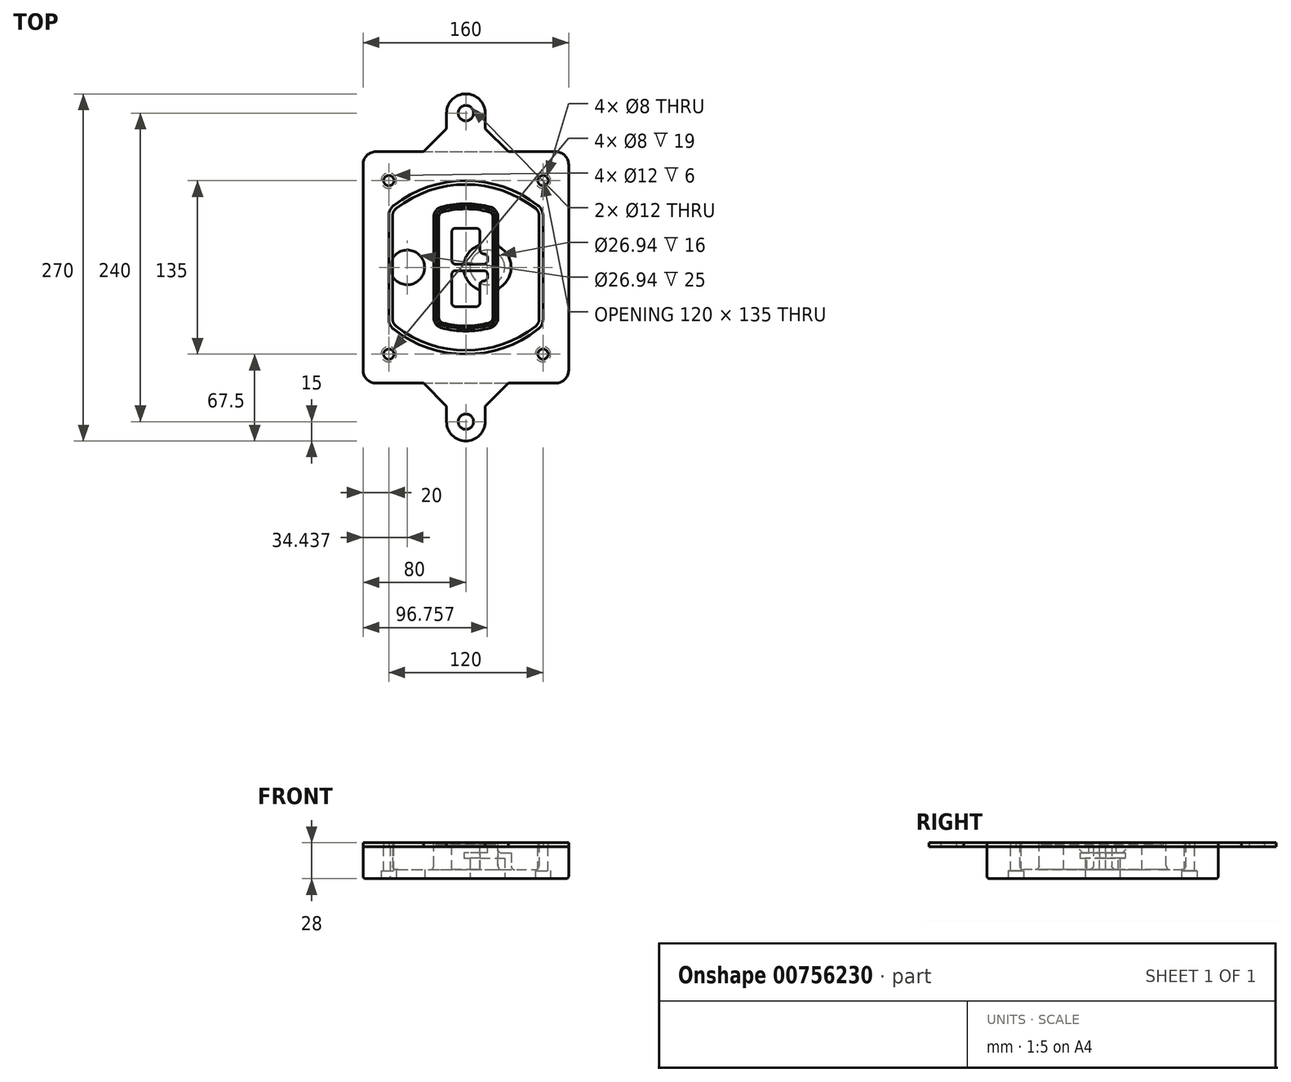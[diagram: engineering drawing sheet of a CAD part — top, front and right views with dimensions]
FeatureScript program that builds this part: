
annotation { "Feature Type Name" : "Feature", "Feature Type Description" : "" }
export const myFeature = defineFeature(function(context is Context, id is Id, definition is map)
    precondition{}
    {
        {
            var Q0;
            Q0=qCreatedBy(makeId("Top.planeOp"),FACE);
            var sketch = newSketch(context, id + "F0", { "sketchPlane" : qUnion([Q0])});
            skPoint(sketch, "E0.rect.middle", {"position": v(0, 0) * mm});
            skLineSegment(sketch, "E1.bottom", {"start": v(-70, -90) * mm, "end": v(70, -90) * mm});
            skLineSegment(sketch, "E1.top", {"start": v(-70, 90) * mm, "end": v(70, 90) * mm});
            skLineSegment(sketch, "E1.left", {"start": v(-80, -80) * mm, "end": v(-80, 80) * mm});
            skLineSegment(sketch, "E1.right", {"start": v(80, -80) * mm, "end": v(80, 80) * mm});
            skLineSegment(sketch, "E2", {"start": v(-80, 90) * mm, "end": v(80, -90) * mm, "construction": true});
            skLineSegment(sketch, "E3", {"start": v(80, 90) * mm, "end": v(-80, -90) * mm, "construction": true});
            skCircle(sketch, "E4", {"center": v(-60, 67.5) * mm, "radius": 4 * mm});
            skCircle(sketch, "E5", {"center": v(60, 67.5) * mm, "radius": 4 * mm});
            skCircle(sketch, "E6", {"center": v(60, -67.5) * mm, "radius": 4 * mm});
            skCircle(sketch, "E7", {"center": v(-60, -67.5) * mm, "radius": 4 * mm});
            skLineSegment(sketch, "E8", {"start": v(-60, 67.5) * mm, "end": v(60, 67.5) * mm, "construction": true});
            skLineSegment(sketch, "E9", {"start": v(60, 67.5) * mm, "end": v(60, -67.5) * mm, "construction": true});
            skLineSegment(sketch, "E10", {"start": v(60, -67.5) * mm, "end": v(-60, -67.5) * mm, "construction": true});
            skLineSegment(sketch, "E11", {"start": v(-60, -67.5) * mm, "end": v(-60, 67.5) * mm, "construction": true});
            skLineSegment(sketch, "E12", {"start": v(-60, 40.3) * mm, "end": v(-60, -40.3) * mm});
            skLineSegment(sketch, "E13", {"start": v(60, 40.3) * mm, "end": v(60, -40.3) * mm});
            skArc(sketch, "E14", {"start": v(56.15, 48.18) * mm, "mid": v(0, 67.5) * mm, "end": v(-56.15, 48.18) * mm});
            skArc(sketch, "E15", {"start": v(-56.15, -48.18) * mm, "mid": v(0, -67.5) * mm, "end": v(56.15, -48.18) * mm});
            skLineSegment(sketch, "E16", {"start": v(-60, 0) * mm, "end": v(60, 0) * mm, "construction": true});
            skPoint(sketch, "E17.visualSharp", {"position": v(-60, -45) * mm});
            skArc(sketch, "E17.filletArc", {"start": v(-60, -40.3) * mm, "mid": v(-58.99, -44.68) * mm, "end": v(-56.15, -48.18) * mm});
            skPoint(sketch, "E18.visualSharp", {"position": v(-60, 45) * mm});
            skArc(sketch, "E18.filletArc", {"start": v(-56.15, 48.18) * mm, "mid": v(-58.99, 44.68) * mm, "end": v(-60, 40.3) * mm});
            skPoint(sketch, "E19.visualSharp", {"position": v(60, 45) * mm});
            skArc(sketch, "E19.filletArc", {"start": v(60, 40.3) * mm, "mid": v(58.99, 44.68) * mm, "end": v(56.15, 48.18) * mm});
            skPoint(sketch, "E20.visualSharp", {"position": v(60, -45) * mm});
            skArc(sketch, "E20.filletArc", {"start": v(56.15, -48.18) * mm, "mid": v(58.99, -44.68) * mm, "end": v(60, -40.3) * mm});
            skPoint(sketch, "E21.visualSharp", {"position": v(-80, 90) * mm});
            skArc(sketch, "E21.filletArc", {"start": v(-70, 90) * mm, "mid": v(-77.07, 87.07) * mm, "end": v(-80, 80) * mm});
            skPoint(sketch, "E22.visualSharp", {"position": v(80, 90) * mm});
            skArc(sketch, "E22.filletArc", {"start": v(80, 80) * mm, "mid": v(77.07, 87.07) * mm, "end": v(70, 90) * mm});
            skPoint(sketch, "E23.visualSharp", {"position": v(80, -90) * mm});
            skArc(sketch, "E23.filletArc", {"start": v(70, -90) * mm, "mid": v(77.07, -87.07) * mm, "end": v(80, -80) * mm});
            skPoint(sketch, "E24.visualSharp", {"position": v(-80, -90) * mm});
            skArc(sketch, "E24.filletArc", {"start": v(-80, -80) * mm, "mid": v(-77.07, -87.07) * mm, "end": v(-70, -90) * mm});
            skArc(sketch, "E25.0", {"start": v(57, 40.3) * mm, "mid": v(56.3, 43.36) * mm, "end": v(54.3, 45.81) * mm});
            skLineSegment(sketch, "E25.1", {"start": v(57, 40.3) * mm, "end": v(57, -40.3) * mm});
            skArc(sketch, "E25.2", {"start": v(54.3, -45.81) * mm, "mid": v(56.3, -43.36) * mm, "end": v(57, -40.3) * mm});
            skArc(sketch, "E25.3", {"start": v(-54.3, -45.81) * mm, "mid": v(0, -64.5) * mm, "end": v(54.3, -45.81) * mm});
            skArc(sketch, "E25.4", {"start": v(-57, -40.3) * mm, "mid": v(-56.3, -43.36) * mm, "end": v(-54.3, -45.81) * mm});
            skArc(sketch, "E25.5", {"start": v(54.3, 45.81) * mm, "mid": v(0, 64.5) * mm, "end": v(-54.3, 45.81) * mm});
            skLineSegment(sketch, "E25.6", {"start": v(-57, 40.3) * mm, "end": v(-57, -40.3) * mm});
            skArc(sketch, "E25.7", {"start": v(-54.3, 45.81) * mm, "mid": v(-56.3, 43.36) * mm, "end": v(-57, 40.3) * mm});
            skArc(sketch, "E26.0", {"start": v(-58.62, 51.33) * mm, "mid": v(-62.58, 46.43) * mm, "end": v(-64, 40.3) * mm});
            skArc(sketch, "E26.1", {"start": v(58.62, 51.33) * mm, "mid": v(0, 71.5) * mm, "end": v(-58.62, 51.33) * mm});
            skArc(sketch, "E26.2", {"start": v(64, 40.3) * mm, "mid": v(62.58, 46.43) * mm, "end": v(58.62, 51.33) * mm});
            skLineSegment(sketch, "E26.3", {"start": v(64, 40.3) * mm, "end": v(64, -40.3) * mm});
            skArc(sketch, "E26.4", {"start": v(58.62, -51.33) * mm, "mid": v(62.58, -46.43) * mm, "end": v(64, -40.3) * mm});
            skLineSegment(sketch, "E26.5", {"start": v(-64, 40.3) * mm, "end": v(-64, -40.3) * mm});
            skArc(sketch, "E26.6", {"start": v(-58.62, -51.33) * mm, "mid": v(0, -71.5) * mm, "end": v(58.62, -51.33) * mm});
            skArc(sketch, "E26.7", {"start": v(-64, -40.3) * mm, "mid": v(-62.58, -46.43) * mm, "end": v(-58.62, -51.33) * mm});
            skSolve(sketch);
        }
        {
            var Q0;
            Q0=makeQuery(id+"F0.imprint","IMPRINT",FACE,{"disambiguationData":[TD([[makeQuery(id+"F0.imprint","IMPRINT",EDGE,{"derivedFrom":sQuery(id+"F0.wireOp",EDGE,"E1.bottom")}),1.0]])]});
            var Q1;
            Q1=makeQuery(id+"F0.imprint","IMPRINT",FACE,{"disambiguationData":[TD([[makeQuery(id+"F0.imprint","IMPRINT",EDGE,{"derivedFrom":sQuery(id+"F0.wireOp",EDGE,"E12")}),1.0]])]});
            var Q2;
            Q2=makeQuery(id+"F0.imprint","IMPRINT",FACE,{"disambiguationData":[TD([[makeQuery(id+"F0.imprint","IMPRINT",EDGE,{"derivedFrom":sQuery(id+"F0.wireOp",EDGE,"E25.0")}),1.0]])]});
            var Q3;
            Q3=makeQuery(id+"F0.imprint","IMPRINT",FACE,{"disambiguationData":[TD([[makeQuery(id+"F0.imprint","IMPRINT",EDGE,{"derivedFrom":sQuery(id+"F0.wireOp",EDGE,"E12")}),-1.0]])]});
            extrude(context, id + "F1", {"entities" : qUnion([Q0, Q1, Q2, Q3]), "oppositeDirection" : true, "depth" : 25 * mm});
        }
        {
            var Q0;
            Q0=makeQuery(id+"F0.imprint","IMPRINT",FACE,{"disambiguationData":[TD([[makeQuery(id+"F0.imprint","IMPRINT",EDGE,{"derivedFrom":sQuery(id+"F0.wireOp",EDGE,"E12")}),1.0]])]});
            extrude(context, id + "F2", {"entities" : qUnion([Q0]), "operationType" : NewBodyOperationType.ADD, "depth" : 3 * mm});
        }
        {
            var Q0;
            Q0=makeQuery(id+"F0.imprint","IMPRINT",FACE,{"disambiguationData":[TD([[makeQuery(id+"F0.imprint","IMPRINT",EDGE,{"derivedFrom":sQuery(id+"F0.wireOp",EDGE,"E25.0")}),1.0]])]});
            extrude(context, id + "F3", {"entities" : qUnion([Q0]), "operationType" : NewBodyOperationType.REMOVE, "oppositeDirection" : true, "depth" : 18 * mm});
        }
        {
            var Q0;
            Q0=makeQuery(id+"F2.opExtrude","CAP_FACE",FACE,{"disambiguationData":[OSD([sQuery(id+"F0.wireOp",EDGE,"E12"),sQuery(id+"F0.wireOp",EDGE,"E13"),sQuery(id+"F0.wireOp",EDGE,"E14"),sQuery(id+"F0.wireOp",EDGE,"E15"),sQuery(id+"F0.wireOp",EDGE,"E17.filletArc"),sQuery(id+"F0.wireOp",EDGE,"E18.filletArc"),sQuery(id+"F0.wireOp",EDGE,"E19.filletArc"),sQuery(id+"F0.wireOp",EDGE,"E20.filletArc"),sQuery(id+"F0.wireOp",EDGE,"E25.0"),sQuery(id+"F0.wireOp",EDGE,"E25.1"),sQuery(id+"F0.wireOp",EDGE,"E25.2"),sQuery(id+"F0.wireOp",EDGE,"E25.3"),sQuery(id+"F0.wireOp",EDGE,"E25.4"),sQuery(id+"F0.wireOp",EDGE,"E25.5"),sQuery(id+"F0.wireOp",EDGE,"E25.6"),sQuery(id+"F0.wireOp",EDGE,"E25.7")])],"isStart":false});
            var sketch = newSketch(context, id + "F4", { "sketchPlane" : qUnion([Q0])});
            skArc(sketch, "E27.0", {"start": v(-19.08, -46.97) * mm, "mid": v(0, -49.5) * mm, "end": v(19.08, -46.97) * mm});
            skArc(sketch, "E28.0", {"start": v(19.08, 46.97) * mm, "mid": v(0, 49.5) * mm, "end": v(-19.08, 46.97) * mm});
            skLineSegment(sketch, "E29", {"start": v(-25, 39.25) * mm, "end": v(-25, -39.25) * mm});
            skLineSegment(sketch, "E30", {"start": v(25, 39.25) * mm, "end": v(25, -39.25) * mm});
            skLineSegment(sketch, "E31", {"start": v(-25, 45.1) * mm, "end": v(25, 45.1) * mm, "construction": true});
            skLineSegment(sketch, "E32", {"start": v(-25, -45.1) * mm, "end": v(25, -45.1) * mm, "construction": true});
            skPoint(sketch, "E33.visualSharp", {"position": v(-25, 45.1) * mm});
            skArc(sketch, "E33.filletArc", {"start": v(-19.08, 46.97) * mm, "mid": v(-23.35, 44.11) * mm, "end": v(-25, 39.25) * mm});
            skPoint(sketch, "E34.visualSharp", {"position": v(25, 45.1) * mm});
            skArc(sketch, "E34.filletArc", {"start": v(25, 39.25) * mm, "mid": v(23.35, 44.11) * mm, "end": v(19.08, 46.97) * mm});
            skPoint(sketch, "E35.visualSharp", {"position": v(25, -45.1) * mm});
            skArc(sketch, "E35.filletArc", {"start": v(19.08, -46.97) * mm, "mid": v(23.35, -44.11) * mm, "end": v(25, -39.25) * mm});
            skPoint(sketch, "E36.visualSharp", {"position": v(-25, -45.1) * mm});
            skArc(sketch, "E36.filletArc", {"start": v(-25, -39.25) * mm, "mid": v(-23.35, -44.11) * mm, "end": v(-19.08, -46.97) * mm});
            skArc(sketch, "E37.0", {"start": v(54.3, 45.81) * mm, "mid": v(0, 64.5) * mm, "end": v(-54.3, 45.81) * mm});
            skArc(sketch, "E37.1", {"start": v(-54.3, 45.81) * mm, "mid": v(-56.3, 43.36) * mm, "end": v(-57, 40.3) * mm});
            skLineSegment(sketch, "E37.2", {"start": v(-57, 40.3) * mm, "end": v(-57, -40.3) * mm});
            skArc(sketch, "E37.3", {"start": v(-57, -40.3) * mm, "mid": v(-56.3, -43.36) * mm, "end": v(-54.3, -45.81) * mm});
            skArc(sketch, "E37.4", {"start": v(-54.3, -45.81) * mm, "mid": v(0, -64.5) * mm, "end": v(54.3, -45.81) * mm});
            skArc(sketch, "E37.5", {"start": v(54.3, -45.81) * mm, "mid": v(56.3, -43.36) * mm, "end": v(57, -40.3) * mm});
            skLineSegment(sketch, "E37.6", {"start": v(57, 40.3) * mm, "end": v(57, -40.3) * mm});
            skArc(sketch, "E37.7", {"start": v(57, 40.3) * mm, "mid": v(56.3, 43.36) * mm, "end": v(54.3, 45.81) * mm});
            skLineSegment(sketch, "E38.0", {"start": v(23, 39.25) * mm, "end": v(23, -39.25) * mm});
            skArc(sketch, "E38.1", {"start": v(18.56, -45.04) * mm, "mid": v(21.76, -42.9) * mm, "end": v(23, -39.25) * mm});
            skArc(sketch, "E38.2", {"start": v(-18.56, -45.04) * mm, "mid": v(0, -47.5) * mm, "end": v(18.56, -45.04) * mm});
            skArc(sketch, "E38.3", {"start": v(-23, -39.25) * mm, "mid": v(-21.76, -42.9) * mm, "end": v(-18.56, -45.04) * mm});
            skLineSegment(sketch, "E38.4", {"start": v(-23, 39.25) * mm, "end": v(-23, -39.25) * mm});
            skArc(sketch, "E38.5", {"start": v(23, 39.25) * mm, "mid": v(21.76, 42.9) * mm, "end": v(18.56, 45.04) * mm});
            skArc(sketch, "E38.6", {"start": v(-18.56, 45.04) * mm, "mid": v(-21.76, 42.9) * mm, "end": v(-23, 39.25) * mm});
            skArc(sketch, "E38.7", {"start": v(18.56, 45.04) * mm, "mid": v(0, 47.5) * mm, "end": v(-18.56, 45.04) * mm});
            skArc(sketch, "E39.0", {"start": v(21, 39.25) * mm, "mid": v(20.18, 41.68) * mm, "end": v(18.04, 43.1) * mm});
            skLineSegment(sketch, "E39.1", {"start": v(21, 39.25) * mm, "end": v(21, -39.25) * mm});
            skArc(sketch, "E39.2", {"start": v(18.04, -43.1) * mm, "mid": v(20.18, -41.68) * mm, "end": v(21, -39.25) * mm});
            skArc(sketch, "E39.3", {"start": v(-18.04, -43.1) * mm, "mid": v(0, -45.5) * mm, "end": v(18.04, -43.1) * mm});
            skArc(sketch, "E39.4", {"start": v(-21, -39.25) * mm, "mid": v(-20.18, -41.68) * mm, "end": v(-18.04, -43.1) * mm});
            skArc(sketch, "E39.5", {"start": v(18.04, 43.1) * mm, "mid": v(0, 45.5) * mm, "end": v(-18.04, 43.1) * mm});
            skLineSegment(sketch, "E39.6", {"start": v(-21, 39.25) * mm, "end": v(-21, -39.25) * mm});
            skArc(sketch, "E39.7", {"start": v(-18.04, 43.1) * mm, "mid": v(-20.18, 41.68) * mm, "end": v(-21, 39.25) * mm});
            skLineSegment(sketch, "E40", {"start": v(-25, 0) * mm, "end": v(25, 0) * mm, "construction": true});
            skLineSegment(sketch, "E41", {"start": v(-11, 5.5) * mm, "end": v(-11, 27.5) * mm});
            skLineSegment(sketch, "E42", {"start": v(-8, 30.5) * mm, "end": v(8, 30.5) * mm});
            skLineSegment(sketch, "E43", {"start": v(11, 27.5) * mm, "end": v(11, 13.5) * mm});
            skLineSegment(sketch, "E44", {"start": v(14, 10.5) * mm, "end": v(14, 10.5) * mm});
            skLineSegment(sketch, "E45", {"start": v(17, 7.5) * mm, "end": v(17, 5.5) * mm});
            skLineSegment(sketch, "E46", {"start": v(14, 2.5) * mm, "end": v(-8, 2.5) * mm});
            skPoint(sketch, "E47.visualSharp", {"position": v(-11, 30.5) * mm});
            skArc(sketch, "E47.filletArc", {"start": v(-8, 30.5) * mm, "mid": v(-10.12, 29.62) * mm, "end": v(-11, 27.5) * mm});
            skPoint(sketch, "E48.visualSharp", {"position": v(11, 30.5) * mm});
            skArc(sketch, "E48.filletArc", {"start": v(11, 27.5) * mm, "mid": v(10.12, 29.62) * mm, "end": v(8, 30.5) * mm});
            skPoint(sketch, "E49.visualSharp", {"position": v(11, 10.5) * mm});
            skArc(sketch, "E49.filletArc", {"start": v(11, 13.5) * mm, "mid": v(11.88, 11.38) * mm, "end": v(14, 10.5) * mm});
            skPoint(sketch, "E50.visualSharp", {"position": v(17, 10.5) * mm});
            skArc(sketch, "E50.filletArc", {"start": v(17, 7.5) * mm, "mid": v(16.12, 9.62) * mm, "end": v(14, 10.5) * mm});
            skPoint(sketch, "E51.visualSharp", {"position": v(17, 2.5) * mm});
            skArc(sketch, "E51.filletArc", {"start": v(14, 2.5) * mm, "mid": v(16.12, 3.38) * mm, "end": v(17, 5.5) * mm});
            skPoint(sketch, "E52.visualSharp", {"position": v(-11, 2.5) * mm});
            skArc(sketch, "E52.filletArc", {"start": v(-11, 5.5) * mm, "mid": v(-10.12, 3.38) * mm, "end": v(-8, 2.5) * mm});
            skLineSegment(sketch, "E53.0.MirrorCS", {"start": v(14, -2.5) * mm, "end": v(-8, -2.5) * mm});
            skArc(sketch, "E54.0.MirrorCS", {"start": v(-11, -5.5) * mm, "mid": v(-10.12, -3.38) * mm, "end": v(-8, -2.5) * mm});
            skLineSegment(sketch, "E55.0.MirrorCS", {"start": v(-11, -5.5) * mm, "end": v(-11, -27.5) * mm});
            skArc(sketch, "E56.0.MirrorCS", {"start": v(-8, -30.5) * mm, "mid": v(-10.12, -29.62) * mm, "end": v(-11, -27.5) * mm});
            skLineSegment(sketch, "E57.0.MirrorCS", {"start": v(-8, -30.5) * mm, "end": v(8, -30.5) * mm});
            skArc(sketch, "E58.0.MirrorCS", {"start": v(11, -27.5) * mm, "mid": v(10.12, -29.62) * mm, "end": v(8, -30.5) * mm});
            skLineSegment(sketch, "E59.0.MirrorCS", {"start": v(11, -27.5) * mm, "end": v(11, -13.5) * mm});
            skArc(sketch, "E60.0.MirrorCS", {"start": v(11, -13.5) * mm, "mid": v(11.88, -11.38) * mm, "end": v(14, -10.5) * mm});
            skArc(sketch, "E61.0.MirrorCS", {"start": v(17, -7.5) * mm, "mid": v(16.12, -9.62) * mm, "end": v(14, -10.5) * mm});
            skLineSegment(sketch, "E62.0.MirrorCS", {"start": v(17, -7.5) * mm, "end": v(17, -5.5) * mm});
            skArc(sketch, "E63.0.MirrorCS", {"start": v(14, -2.5) * mm, "mid": v(16.12, -3.38) * mm, "end": v(17, -5.5) * mm});
            skSolve(sketch);
        }
        {
            var Q0;
            Q0=makeQuery(id+"F4.imprint","IMPRINT",FACE,{"disambiguationData":[TD([[makeQuery(id+"F4.imprint","IMPRINT",EDGE,{"derivedFrom":sQuery(id+"F4.wireOp",EDGE,"E27.0")}),1.0]])]});
            var Q1;
            Q1=makeQuery(id+"F4.imprint","IMPRINT",FACE,{"disambiguationData":[TD([[makeQuery(id+"F4.imprint","IMPRINT",EDGE,{"derivedFrom":sQuery(id+"F4.wireOp",EDGE,"E38.0")}),-1.0]])]});
            var Q2;
            Q2=makeQuery(id+"F4.imprint","IMPRINT",FACE,{"disambiguationData":[TD([[makeQuery(id+"F4.imprint","IMPRINT",EDGE,{"derivedFrom":sQuery(id+"F4.wireOp",EDGE,"E39.0")}),1.0]])]});
            extrude(context, id + "F5", {"entities" : qUnion([Q0, Q1, Q2]), "operationType" : NewBodyOperationType.ADD, "endBound" : BoundingType.UP_TO_NEXT, "oppositeDirection" : true, "depth" : 25 * mm});
        }
        {
            var Q0;
            Q0=makeQuery(id+"F4.imprint","IMPRINT",FACE,{"disambiguationData":[TD([[makeQuery(id+"F4.imprint","IMPRINT",EDGE,{"derivedFrom":sQuery(id+"F4.wireOp",EDGE,"E38.0")}),-1.0]])]});
            extrude(context, id + "F6", {"entities" : qUnion([Q0]), "operationType" : NewBodyOperationType.REMOVE, "oppositeDirection" : true, "depth" : 2 * mm});
        }
        {
            var Q0;
            Q0=makeQuery(id+"F1.opExtrude","CAP_FACE",FACE,{"disambiguationData":[OSD([sQuery(id+"F0.wireOp",EDGE,"E1.bottom"),sQuery(id+"F0.wireOp",EDGE,"E1.top"),sQuery(id+"F0.wireOp",EDGE,"E1.left"),sQuery(id+"F0.wireOp",EDGE,"E1.right"),sQuery(id+"F0.wireOp",EDGE,"E4"),sQuery(id+"F0.wireOp",EDGE,"E5"),sQuery(id+"F0.wireOp",EDGE,"E6"),sQuery(id+"F0.wireOp",EDGE,"E7"),sQuery(id+"F0.wireOp",EDGE,"E21.filletArc"),sQuery(id+"F0.wireOp",EDGE,"E22.filletArc"),sQuery(id+"F0.wireOp",EDGE,"E23.filletArc"),sQuery(id+"F0.wireOp",EDGE,"E24.filletArc")])],"isStart":false});
            var sketch = newSketch(context, id + "F7", { "sketchPlane" : qUnion([Q0])});
            skCircle(sketch, "E64", {"center": v(16.76, 0) * mm, "radius": 13.47 * mm});
            skCircle(sketch, "E65", {"center": v(-45.56, 0) * mm, "radius": 13.47 * mm});
            skLineSegment(sketch, "E66", {"start": v(80, 0) * mm, "end": v(-80, 0) * mm});
            skCircle(sketch, "E67", {"center": v(16.76, 0) * mm, "radius": 18.47 * mm});
            skCircle(sketch, "E68", {"center": v(60, -67.5) * mm, "radius": 6 * mm});
            skCircle(sketch, "E69", {"center": v(-60, -67.5) * mm, "radius": 6 * mm});
            skCircle(sketch, "E70", {"center": v(-60, 67.5) * mm, "radius": 6 * mm});
            skCircle(sketch, "E71", {"center": v(60, 67.5) * mm, "radius": 6 * mm});
            skSolve(sketch);
        }
        {
            var Q0;
            {var subQ1=sQuery(id+"F7.wireOp",EDGE,"E66");var subQ4=sQuery(id+"F7.wireOp",EDGE,"E64");var subQ6=makeQuery(id+"F7.imprint","INTERSECT",VERTEX,{"disambiguationData":[OD(0.0)],"derivedFrom":[subQ4,subQ1]});Q0=makeQuery(id+"F7.imprint","IMPRINT",FACE,{"disambiguationData":[TD([[makeQuery(id+"F7.imprint","IMPRINT",EDGE,{"disambiguationData":[TD([[subQ6,-1.0]])],"derivedFrom":subQ4}),-1.0]])]});}
            var Q1;
            {var subQ0=sQuery(id+"F7.wireOp",EDGE,"E66");var subQ1=sQuery(id+"F7.wireOp",EDGE,"E64");var subQ3=makeQuery(id+"F7.imprint","INTERSECT",VERTEX,{"disambiguationData":[OD(0.0)],"derivedFrom":[subQ1,subQ0]});Q1=makeQuery(id+"F7.imprint","IMPRINT",FACE,{"disambiguationData":[TD([[makeQuery(id+"F7.imprint","IMPRINT",EDGE,{"disambiguationData":[TD([[subQ3,-1.0]])],"derivedFrom":subQ1}),1.0]])]});}
            var Q2;
            {var subQ0=sQuery(id+"F7.wireOp",EDGE,"E66");var subQ1=sQuery(id+"F7.wireOp",EDGE,"E64");var subQ3=makeQuery(id+"F7.imprint","INTERSECT",VERTEX,{"disambiguationData":[OD(0.0)],"derivedFrom":[subQ1,subQ0]});Q2=makeQuery(id+"F7.imprint","IMPRINT",FACE,{"disambiguationData":[TD([[makeQuery(id+"F7.imprint","IMPRINT",EDGE,{"disambiguationData":[TD([[subQ3,1.0]])],"derivedFrom":subQ1}),1.0]])]});}
            var Q3;
            {var subQ1=sQuery(id+"F7.wireOp",EDGE,"E66");var subQ4=sQuery(id+"F7.wireOp",EDGE,"E64");var subQ6=makeQuery(id+"F7.imprint","INTERSECT",VERTEX,{"disambiguationData":[OD(0.0)],"derivedFrom":[subQ4,subQ1]});Q3=makeQuery(id+"F7.imprint","IMPRINT",FACE,{"disambiguationData":[TD([[makeQuery(id+"F7.imprint","IMPRINT",EDGE,{"disambiguationData":[TD([[subQ6,1.0]])],"derivedFrom":subQ4}),-1.0]])]});}
            extrude(context, id + "F8", {"entities" : qUnion([Q0, Q1, Q2, Q3]), "operationType" : NewBodyOperationType.ADD, "oppositeDirection" : true, "depth" : 20 * mm});
        }
        {
            var Q0;
            {var subQ0=sQuery(id+"F7.wireOp",EDGE,"E66");var subQ1=sQuery(id+"F7.wireOp",EDGE,"E64");var subQ3=makeQuery(id+"F7.imprint","INTERSECT",VERTEX,{"disambiguationData":[OD(0.0)],"derivedFrom":[subQ1,subQ0]});Q0=makeQuery(id+"F7.imprint","IMPRINT",FACE,{"disambiguationData":[TD([[makeQuery(id+"F7.imprint","IMPRINT",EDGE,{"disambiguationData":[TD([[subQ3,-1.0]])],"derivedFrom":subQ1}),1.0]])]});}
            var Q1;
            {var subQ0=sQuery(id+"F7.wireOp",EDGE,"E66");var subQ1=sQuery(id+"F7.wireOp",EDGE,"E64");var subQ3=makeQuery(id+"F7.imprint","INTERSECT",VERTEX,{"disambiguationData":[OD(0.0)],"derivedFrom":[subQ1,subQ0]});Q1=makeQuery(id+"F7.imprint","IMPRINT",FACE,{"disambiguationData":[TD([[makeQuery(id+"F7.imprint","IMPRINT",EDGE,{"disambiguationData":[TD([[subQ3,1.0]])],"derivedFrom":subQ1}),1.0]])]});}
            extrude(context, id + "F9", {"entities" : qUnion([Q0, Q1]), "operationType" : NewBodyOperationType.REMOVE, "oppositeDirection" : true, "depth" : 16 * mm});
        }
        {
            var Q0;
            {var subQ0=sQuery(id+"F7.wireOp",EDGE,"E66");var subQ1=sQuery(id+"F7.wireOp",EDGE,"E65");var subQ3=makeQuery(id+"F7.imprint","INTERSECT",VERTEX,{"disambiguationData":[OD(0.0)],"derivedFrom":[subQ1,subQ0]});Q0=makeQuery(id+"F7.imprint","IMPRINT",FACE,{"disambiguationData":[TD([[makeQuery(id+"F7.imprint","IMPRINT",EDGE,{"disambiguationData":[TD([[subQ3,-1.0]])],"derivedFrom":subQ1}),1.0]])]});}
            var Q1;
            {var subQ0=sQuery(id+"F7.wireOp",EDGE,"E66");var subQ1=sQuery(id+"F7.wireOp",EDGE,"E65");var subQ3=makeQuery(id+"F7.imprint","INTERSECT",VERTEX,{"disambiguationData":[OD(0.0)],"derivedFrom":[subQ1,subQ0]});Q1=makeQuery(id+"F7.imprint","IMPRINT",FACE,{"disambiguationData":[TD([[makeQuery(id+"F7.imprint","IMPRINT",EDGE,{"disambiguationData":[TD([[subQ3,1.0]])],"derivedFrom":subQ1}),1.0]])]});}
            extrude(context, id + "F10", {"entities" : qUnion([Q0, Q1]), "operationType" : NewBodyOperationType.REMOVE, "oppositeDirection" : true, "depth" : 25 * mm});
        }
        {
            var Q0;
            Q0=makeQuery(id+"F7.imprint","IMPRINT",FACE,{"disambiguationData":[TD([[makeQuery(id+"F7.imprint","IMPRINT",EDGE,{"derivedFrom":sQuery(id+"F7.wireOp",EDGE,"E68")}),1.0]])]});
            var Q1;
            Q1=makeQuery(id+"F7.imprint","IMPRINT",FACE,{"disambiguationData":[TD([[makeQuery(id+"F7.imprint","IMPRINT",EDGE,{"derivedFrom":makeQuery(id+"F1.opExtrude","CAP_EDGE",EDGE,{"disambiguationData":[OSD([sQuery(id+"F0.wireOp",EDGE,"E5")])],"isStart":false})}),-1.0]])]});
            var Q2;
            Q2=makeQuery(id+"F7.imprint","IMPRINT",FACE,{"disambiguationData":[TD([[makeQuery(id+"F7.imprint","IMPRINT",EDGE,{"derivedFrom":sQuery(id+"F7.wireOp",EDGE,"E69")}),1.0]])]});
            var Q3;
            Q3=makeQuery(id+"F7.imprint","IMPRINT",FACE,{"disambiguationData":[TD([[makeQuery(id+"F7.imprint","IMPRINT",EDGE,{"derivedFrom":makeQuery(id+"F1.opExtrude","CAP_EDGE",EDGE,{"disambiguationData":[OSD([sQuery(id+"F0.wireOp",EDGE,"E4")])],"isStart":false})}),-1.0]])]});
            var Q4;
            Q4=makeQuery(id+"F7.imprint","IMPRINT",FACE,{"disambiguationData":[TD([[makeQuery(id+"F7.imprint","IMPRINT",EDGE,{"derivedFrom":sQuery(id+"F7.wireOp",EDGE,"E70")}),1.0]])]});
            var Q5;
            Q5=makeQuery(id+"F7.imprint","IMPRINT",FACE,{"disambiguationData":[TD([[makeQuery(id+"F7.imprint","IMPRINT",EDGE,{"derivedFrom":makeQuery(id+"F1.opExtrude","CAP_EDGE",EDGE,{"disambiguationData":[OSD([sQuery(id+"F0.wireOp",EDGE,"E7")])],"isStart":false})}),-1.0]])]});
            var Q6;
            Q6=makeQuery(id+"F7.imprint","IMPRINT",FACE,{"disambiguationData":[TD([[makeQuery(id+"F7.imprint","IMPRINT",EDGE,{"derivedFrom":sQuery(id+"F7.wireOp",EDGE,"E71")}),1.0]])]});
            var Q7;
            Q7=makeQuery(id+"F7.imprint","IMPRINT",FACE,{"disambiguationData":[TD([[makeQuery(id+"F7.imprint","IMPRINT",EDGE,{"derivedFrom":makeQuery(id+"F1.opExtrude","CAP_EDGE",EDGE,{"disambiguationData":[OSD([sQuery(id+"F0.wireOp",EDGE,"E6")])],"isStart":false})}),-1.0]])]});
            extrude(context, id + "F11", {"entities" : qUnion([Q0, Q1, Q2, Q3, Q4, Q5, Q6, Q7]), "operationType" : NewBodyOperationType.REMOVE, "oppositeDirection" : true, "depth" : 6 * mm});
        }
        {
            var Q0;
            Q0=makeQuery(id+"F9.boolean.opBoolean","COPY",FACE,{"derivedFrom":makeQuery(id+"F9.opExtrude","CAP_FACE",FACE,{"disambiguationData":[OSD([sQuery(id+"F7.wireOp",EDGE,"E64")])],"isStart":false})});
            var sketch = newSketch(context, id + "F12", { "sketchPlane" : qUnion([Q0])});
            skArc(sketch, "E72.0", {"start": v(11, 17.55) * mm, "mid": v(2.57, 11.82) * mm, "end": v(-1.54, 2.5) * mm});
            skArc(sketch, "E72.1", {"start": v(-1.54, -2.5) * mm, "mid": v(2.57, -11.82) * mm, "end": v(11, -17.55) * mm});
            skLineSegment(sketch, "E73", {"start": v(-1.54, -2.5) * mm, "end": v(14, -2.5) * mm});
            skLineSegment(sketch, "E74.0", {"start": v(14, 2.5) * mm, "end": v(-1.54, 2.5) * mm});
            skArc(sketch, "E74.1", {"start": v(14, 2.5) * mm, "mid": v(16.12, 3.38) * mm, "end": v(17, 5.5) * mm});
            skLineSegment(sketch, "E74.2", {"start": v(17, 7.5) * mm, "end": v(17, 5.5) * mm});
            skArc(sketch, "E74.3", {"start": v(17, 7.5) * mm, "mid": v(16.12, 9.62) * mm, "end": v(14, 10.5) * mm});
            skArc(sketch, "E74.4", {"start": v(11, 13.5) * mm, "mid": v(11.88, 11.38) * mm, "end": v(14, 10.5) * mm});
            skLineSegment(sketch, "E74.5", {"start": v(11, 17.55) * mm, "end": v(11, 13.5) * mm});
            skLineSegment(sketch, "E74.7", {"start": v(14, -2.5) * mm, "end": v(-1.54, -2.5) * mm});
            skArc(sketch, "E74.8", {"start": v(14, -2.5) * mm, "mid": v(16.12, -3.38) * mm, "end": v(17, -5.5) * mm});
            skLineSegment(sketch, "E74.9", {"start": v(17, -7.5) * mm, "end": v(17, -5.5) * mm});
            skArc(sketch, "E74.10", {"start": v(17, -7.5) * mm, "mid": v(16.12, -9.62) * mm, "end": v(14, -10.5) * mm});
            skArc(sketch, "E74.11", {"start": v(11, -13.5) * mm, "mid": v(11.88, -11.38) * mm, "end": v(14, -10.5) * mm});
            skLineSegment(sketch, "E74.12", {"start": v(11, -17.55) * mm, "end": v(11, -13.5) * mm});
            skPoint(sketch, "E75.orphan", {"position": v(11, -27.5) * mm});
            skPoint(sketch, "E76.orphan", {"position": v(-8, -2.5) * mm});
            skPoint(sketch, "E77.orphan", {"position": v(-8, 2.5) * mm});
            skPoint(sketch, "E78.orphan", {"position": v(11, 27.5) * mm});
            skSolve(sketch);
        }
        {
            var Q0;
            {var subQ7=sQuery(id+"F12.wireOp",EDGE,"E72.0");var subQ14=sQuery(id+"F12.wireOp",EDGE,"E72.1");var subQ16=sQuery(id+"F12.wireOp",EDGE,"E74.1");var subQ18=sQuery(id+"F12.wireOp",EDGE,"E74.8");Q0=qUnion([makeQuery(id+"F12.imprint","IMPRINT",FACE,{"disambiguationData":[TD([[makeQuery(id+"F12.imprint","IMPRINT",EDGE,{"derivedFrom":subQ7}),1.0]])]}),makeQuery(id+"F12.imprint","IMPRINT",FACE,{"disambiguationData":[TD([[makeQuery(id+"F12.imprint","IMPRINT",EDGE,{"derivedFrom":subQ14}),1.0]])]}),makeQuery(id+"F12.imprint","IMPRINT",FACE,{"disambiguationData":[TD([[makeQuery(id+"F12.imprint","IMPRINT",EDGE,{"derivedFrom":subQ16}),1.0]])]}),makeQuery(id+"F12.imprint","IMPRINT",FACE,{"disambiguationData":[TD([[makeQuery(id+"F12.imprint","IMPRINT",EDGE,{"derivedFrom":subQ18}),-1.0]])]})]);}
            var Q1;
            Q1=makeQuery(id+"F5.boolean.opBoolean","SPLIT",FACE,{"disambiguationData":[TD([makeQuery(id+"F5.opExtrude","SWEPT_FACE",FACE,{"disambiguationData":[OSD([sQuery(id+"F4.wireOp",EDGE,"E41")])]})])],"derivedFrom":makeQuery(id+"F3.boolean.opBoolean","COPY",FACE,{"derivedFrom":makeQuery(id+"F3.opExtrude","CAP_FACE",FACE,{"disambiguationData":[OSD([sQuery(id+"F0.wireOp",EDGE,"E25.0"),sQuery(id+"F0.wireOp",EDGE,"E25.1"),sQuery(id+"F0.wireOp",EDGE,"E25.2"),sQuery(id+"F0.wireOp",EDGE,"E25.3"),sQuery(id+"F0.wireOp",EDGE,"E25.4"),sQuery(id+"F0.wireOp",EDGE,"E25.5"),sQuery(id+"F0.wireOp",EDGE,"E25.6"),sQuery(id+"F0.wireOp",EDGE,"E25.7")])],"isStart":false})})});
            extrude(context, id + "F13", {"entities" : qUnion([Q0]), "operationType" : NewBodyOperationType.REMOVE, "endBound" : BoundingType.UP_TO_SURFACE, "endBoundEntityFace" : qUnion([Q1]), "depth" : 25 * mm});
        }
        {
            var Q0;
            Q0=makeQuery(id+"F3.boolean.opBoolean","COPY",EDGE,{"derivedFrom":makeQuery(id+"F3.opExtrude","CAP_EDGE",EDGE,{"disambiguationData":[OSD([sQuery(id+"F0.wireOp",EDGE,"E25.6")])],"isStart":false})});
            var Q1;
            Q1=makeQuery(id+"F8.boolean.opBoolean","INTERSECT",EDGE,{"derivedFrom":[makeQuery(id+"F5.opExtrude","SWEPT_FACE",FACE,{"disambiguationData":[OSD([sQuery(id+"F4.wireOp",EDGE,"E30")])]}),makeQuery(id+"F8.opExtrude","CAP_FACE",FACE,{"disambiguationData":[OSD([sQuery(id+"F7.wireOp",EDGE,"E67")])],"isStart":false})]});
            var Q2;
            Q2=makeQuery(id+"F8.boolean.opBoolean","INTERSECT",EDGE,{"disambiguationData":[OD(1.0)],"derivedFrom":[makeQuery(id+"F5.opExtrude","SWEPT_FACE",FACE,{"disambiguationData":[OSD([sQuery(id+"F4.wireOp",EDGE,"E30")])]}),makeQuery(id+"F8.opExtrude","SWEPT_FACE",FACE,{"disambiguationData":[OSD([sQuery(id+"F7.wireOp",EDGE,"E67")])]})]});
            var Q3;
            {var subQ0=sQuery(id+"F4.wireOp",EDGE,"E30");Q3=makeQuery(id+"F8.boolean.opBoolean","SPLIT",EDGE,{"disambiguationData":[TD([makeQuery(id+"F5.opExtrude","SWEPT_FACE",FACE,{"disambiguationData":[OSD([sQuery(id+"F4.wireOp",EDGE,"E35.filletArc")])]})])],"derivedFrom":makeQuery(id+"F5.opExtrude","CAP_EDGE",EDGE,{"disambiguationData":[OSD([subQ0])],"isStart":false})});}
            var Q4;
            {var subQ0=sQuery(id+"F0.wireOp",EDGE,"E25.7");var subQ1=sQuery(id+"F0.wireOp",EDGE,"E25.1");var subQ2=sQuery(id+"F0.wireOp",EDGE,"E25.6");var subQ3=sQuery(id+"F0.wireOp",EDGE,"E25.5");var subQ4=sQuery(id+"F0.wireOp",EDGE,"E25.4");var subQ5=sQuery(id+"F0.wireOp",EDGE,"E25.0");var subQ6=sQuery(id+"F0.wireOp",EDGE,"E25.2");var subQ7=sQuery(id+"F0.wireOp",EDGE,"E25.3");Q4=makeQuery(id+"F8.boolean.opBoolean","INTERSECT",EDGE,{"derivedFrom":[makeQuery(id+"F5.boolean.opBoolean","SPLIT",FACE,{"disambiguationData":[TD([makeQuery(id+"F2.opExtrude","SWEPT_FACE",FACE,{"disambiguationData":[OSD([subQ5])]})])],"derivedFrom":makeQuery(id+"F3.boolean.opBoolean","COPY",FACE,{"derivedFrom":makeQuery(id+"F3.opExtrude","CAP_FACE",FACE,{"disambiguationData":[OSD([subQ5,subQ1,subQ6,subQ7,subQ4,subQ3,subQ2,subQ0])],"isStart":false})})}),makeQuery(id+"F8.opExtrude","SWEPT_FACE",FACE,{"disambiguationData":[OSD([sQuery(id+"F7.wireOp",EDGE,"E67")])]})]});}
            var Q5;
            Q5=makeQuery(id+"F8.boolean.opBoolean","INTERSECT",EDGE,{"disambiguationData":[OD(0.0)],"derivedFrom":[makeQuery(id+"F5.opExtrude","SWEPT_FACE",FACE,{"disambiguationData":[OSD([sQuery(id+"F4.wireOp",EDGE,"E30")])]}),makeQuery(id+"F8.opExtrude","SWEPT_FACE",FACE,{"disambiguationData":[OSD([sQuery(id+"F7.wireOp",EDGE,"E67")])]})]});
            fillet(context, id + "F14", {"entities" : qUnion([Q0, Q1, Q2, Q3, Q4, Q5]), "radius" : 3 * mm, "tangentPropagation" : true, "allowEdgeOverflow" : false});
        }
        {
            var Q0;
            Q0=makeQuery(id+"F1.opExtrude","CAP_EDGE",EDGE,{"disambiguationData":[OSD([sQuery(id+"F0.wireOp",EDGE,"E1.bottom")])],"isStart":false});
            fillet(context, id + "F15", {"entities" : qUnion([Q0]), "radius" : 2 * mm, "tangentPropagation" : true, "allowEdgeOverflow" : false});
        }
        {
            var Q0;
            {var subQ0=sQuery(id+"F0.wireOp",EDGE,"E21.filletArc");var subQ1=sQuery(id+"F0.wireOp",EDGE,"E7");var subQ2=sQuery(id+"F0.wireOp",EDGE,"E6");var subQ3=sQuery(id+"F0.wireOp",EDGE,"E5");var subQ4=sQuery(id+"F0.wireOp",EDGE,"E4");var subQ5=sQuery(id+"F0.wireOp",EDGE,"E22.filletArc");var subQ6=sQuery(id+"F0.wireOp",EDGE,"E1.bottom");var subQ7=sQuery(id+"F0.wireOp",EDGE,"E1.right");var subQ8=sQuery(id+"F0.wireOp",EDGE,"E1.top");var subQ9=sQuery(id+"F0.wireOp",EDGE,"E1.left");var subQ10=sQuery(id+"F0.wireOp",EDGE,"E23.filletArc");var subQ11=sQuery(id+"F0.wireOp",EDGE,"E24.filletArc");Q0=makeQuery(id+"F2.boolean.opBoolean","SPLIT",FACE,{"disambiguationData":[TD([makeQuery(id+"F1.opExtrude","SWEPT_FACE",FACE,{"disambiguationData":[OSD([subQ6])]})])],"derivedFrom":makeQuery(id+"F1.opExtrude","CAP_FACE",FACE,{"disambiguationData":[OSD([subQ6,subQ8,subQ9,subQ7,subQ4,subQ3,subQ2,subQ1,subQ0,subQ5,subQ10,subQ11])],"isStart":true})});}
            var sketch = newSketch(context, id + "F16", { "sketchPlane" : qUnion([Q0])});
            skPoint(sketch, "E79.startSnap0", {"position": v(0, 90) * mm});
            skLineSegment(sketch, "E80", {"start": v(0, 90) * mm, "end": v(0, 120) * mm, "construction": true});
            skCircle(sketch, "E81", {"center": v(0, 120) * mm, "radius": 6 * mm});
            skLineSegment(sketch, "E82", {"start": v(15, 120) * mm, "end": v(15, 108) * mm});
            skLineSegment(sketch, "E83", {"start": v(15, 108) * mm, "end": v(33, 90) * mm});
            skLineSegment(sketch, "E84", {"start": v(33, 90) * mm, "end": v(-33, 90) * mm});
            skLineSegment(sketch, "E85", {"start": v(-33, 90) * mm, "end": v(-15, 108) * mm});
            skLineSegment(sketch, "E86", {"start": v(-15, 108) * mm, "end": v(-15, 120) * mm});
            skArc(sketch, "E87", {"start": v(15, 120) * mm, "mid": v(0, 135) * mm, "end": v(-15, 120) * mm});
            skLineSegment(sketch, "E88", {"start": v(80, 0) * mm, "end": v(-80, 0) * mm, "construction": true});
            skLineSegment(sketch, "E89.MirrorCS", {"start": v(15, -108) * mm, "end": v(33, -90) * mm});
            skLineSegment(sketch, "E90.MirrorCS", {"start": v(15, -120) * mm, "end": v(15, -108) * mm});
            skArc(sketch, "E91.MirrorCS", {"start": v(15, -120) * mm, "mid": v(0, -135) * mm, "end": v(-15, -120) * mm});
            skCircle(sketch, "E92.MirrorC", {"center": v(0, -120) * mm, "radius": 6 * mm});
            skLineSegment(sketch, "E93.MirrorCS", {"start": v(-33, -90) * mm, "end": v(-15, -108) * mm});
            skLineSegment(sketch, "E94.MirrorCS", {"start": v(-15, -108) * mm, "end": v(-15, -120) * mm});
            skLineSegment(sketch, "E95.MirrorCS", {"start": v(33, -90) * mm, "end": v(-33, -90) * mm});
            skLineSegment(sketch, "E96.MirrorCS", {"start": v(0, -90) * mm, "end": v(0, -120) * mm, "construction": true});
            skSolve(sketch);
        }
        {
            var Q0;
            Q0=makeQuery(id+"F16.imprint","IMPRINT",FACE,{"disambiguationData":[TD([[makeQuery(id+"F16.imprint","IMPRINT",EDGE,{"derivedFrom":sQuery(id+"F16.wireOp",EDGE,"E81")}),-1.0]])]});
            var Q1;
            {var subQ4=sQuery(id+"F16.wireOp",EDGE,"E84");Q1=makeQuery(id+"F16.imprint","IMPRINT",FACE,{"disambiguationData":[TD([[makeQuery(id+"F16.imprint","IMPRINT",EDGE,{"derivedFrom":subQ4}),-1.0]])]});}
            var Q2;
            Q2=makeQuery(id+"F16.imprint","IMPRINT",FACE,{"disambiguationData":[TD([[makeQuery(id+"F16.imprint","IMPRINT",EDGE,{"derivedFrom":sQuery(id+"F16.wireOp",EDGE,"E89.MirrorCS")}),1.0]])]});
            var Q3;
            Q3=makeQuery(id+"F2.opExtrude","CAP_FACE",FACE,{"disambiguationData":[OSD([sQuery(id+"F0.wireOp",EDGE,"E12"),sQuery(id+"F0.wireOp",EDGE,"E13"),sQuery(id+"F0.wireOp",EDGE,"E14"),sQuery(id+"F0.wireOp",EDGE,"E15"),sQuery(id+"F0.wireOp",EDGE,"E17.filletArc"),sQuery(id+"F0.wireOp",EDGE,"E18.filletArc"),sQuery(id+"F0.wireOp",EDGE,"E19.filletArc"),sQuery(id+"F0.wireOp",EDGE,"E20.filletArc"),sQuery(id+"F0.wireOp",EDGE,"E25.0"),sQuery(id+"F0.wireOp",EDGE,"E25.1"),sQuery(id+"F0.wireOp",EDGE,"E25.2"),sQuery(id+"F0.wireOp",EDGE,"E25.3"),sQuery(id+"F0.wireOp",EDGE,"E25.4"),sQuery(id+"F0.wireOp",EDGE,"E25.5"),sQuery(id+"F0.wireOp",EDGE,"E25.6"),sQuery(id+"F0.wireOp",EDGE,"E25.7")])],"isStart":false});
            extrude(context, id + "F17", {"entities" : qUnion([Q0, Q1, Q2]), "endBound" : BoundingType.UP_TO_SURFACE, "depth" : 25 * mm, "endBoundEntityFace" : qUnion([Q3]), "offsetDistance" : 25 * mm});
        }
    });
